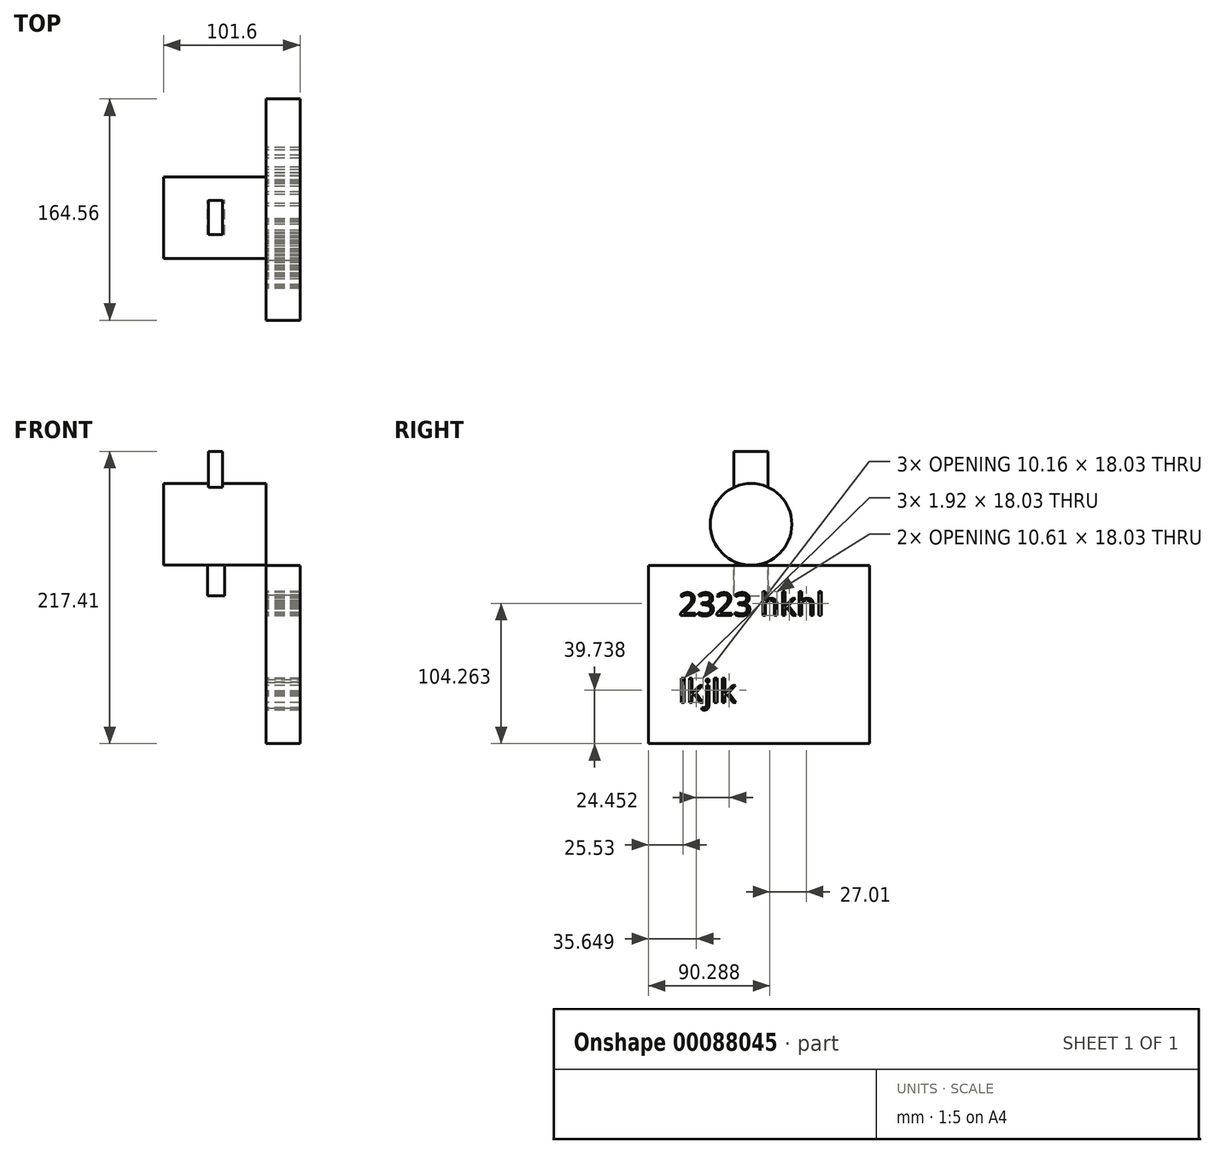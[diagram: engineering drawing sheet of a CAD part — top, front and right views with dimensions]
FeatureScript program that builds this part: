
annotation { "Feature Type Name" : "Feature", "Feature Type Description" : "" }
export const myFeature = defineFeature(function(context is Context, id is Id, definition is map)
    precondition{}
    {
        {
            var Q0;
            Q0=qCreatedBy(makeId("Right.planeOp"),FACE);
            var sketch = newSketch(context, id + "F0", { "sketchPlane" : qUnion([Q0])});
            skCircle(sketch, "E0", {"center": v(0, 0) * mm, "radius": 30.36 * mm});
            skSolve(sketch);
        }
        {
            var Q0;
            Q0 = qSketchRegion(id + "F0", true);
            extrude(context, id + "F1", {"entities" : qUnion([Q0]), "endBound" : BoundingType.SYMMETRIC, "depth" : 76.2 * mm});
        }
        {
            var Q0;
            Q0=qCreatedBy(makeId("Front.planeOp"),FACE);
            var sketch = newSketch(context, id + "F2", { "sketchPlane" : qUnion([Q0])});
            skLineSegment(sketch, "E1", {"start": v(38.1, -30.36) * mm, "end": v(-38.1, -30.36) * mm});
            skLineSegment(sketch, "E2", {"start": v(-5.4, -30.36) * mm, "end": v(-5.4, -52.98) * mm});
            skLineSegment(sketch, "E3", {"start": v(-5.4, -52.98) * mm, "end": v(7.36, -52.98) * mm});
            skLineSegment(sketch, "E4", {"start": v(7.36, -52.98) * mm, "end": v(7.36, -30.36) * mm});
            skLineSegment(sketch, "E5", {"start": v(7.36, -30.36) * mm, "end": v(-5.4, -30.36) * mm});
            skSolve(sketch);
        }
        {
            var Q0;
            Q0 = qSketchRegion(id + "F2", true);
            extrude(context, id + "F3", {"entities" : qUnion([Q0]), "operationType" : NewBodyOperationType.ADD, "endBound" : BoundingType.SYMMETRIC, "depth" : 25.4 * mm});
        }
        {
            var Q0;
            Q0=qCreatedBy(makeId("Front.planeOp"),FACE);
            var sketch = newSketch(context, id + "F4", { "sketchPlane" : qUnion([Q0])});
            skLineSegment(sketch, "E6.bottom", {"start": v(-4.74, 19.3) * mm, "end": v(5.72, 19.3) * mm});
            skLineSegment(sketch, "E6.top", {"start": v(-4.74, 54.28) * mm, "end": v(5.72, 54.28) * mm});
            skLineSegment(sketch, "E6.left", {"start": v(-4.74, 19.3) * mm, "end": v(-4.74, 54.28) * mm});
            skLineSegment(sketch, "E6.right", {"start": v(5.72, 19.3) * mm, "end": v(5.72, 54.28) * mm});
            skSolve(sketch);
        }
        {
            var Q0;
            Q0 = qSketchRegion(id + "F4", true);
            extrude(context, id + "F5", {"entities" : qUnion([Q0]), "operationType" : NewBodyOperationType.ADD, "endBound" : BoundingType.SYMMETRIC, "depth" : 25.4 * mm});
        }
        {
            var Q0;
            Q0=makeQuery(id+"F1.opExtrude","CAP_FACE",FACE,{"disambiguationData":[OSD([sQuery(id+"F0.wireOp",EDGE,"E0")])],"isStart":false});
            var sketch = newSketch(context, id + "F6", { "sketchPlane" : qUnion([Q0])});
            skText(sketch, "E7", { "text": "2323 hkhl\n\nlkjlk", "fontName": "OpenSans-Regular.ttf"});
            skLineSegment(sketch, "E8.bottom", {"start": v(-76.27, -30.49) * mm, "end": v(88.3, -30.49) * mm});
            skLineSegment(sketch, "E8.top", {"start": v(-76.27, -163.13) * mm, "end": v(88.3, -163.13) * mm});
            skLineSegment(sketch, "E8.left", {"start": v(-76.27, -30.49) * mm, "end": v(-76.27, -163.13) * mm});
            skLineSegment(sketch, "E8.right", {"start": v(88.3, -30.49) * mm, "end": v(88.3, -163.13) * mm});
            const initialGuessF6  = {"E7": [-0.05374, -0.06788, 1, 0, 0.01708]};
            skSetInitialGuess(sketch, initialGuessF6);
            skSolve(sketch);
        }
        {
            var Q0;
            Q0 = qSketchRegion(id + "F6", true);
            extrude(context, id + "F7", {"entities" : qUnion([Q0]), "depth" : 25.4 * mm});
        }
    });
